# Revit family: 46-70-010-DN50-600
name_source: partatom
category: Pipe Accessories
units: mm (PartAtom-declared; Revit-internal decimal feet)

## family parameters
Always vertical = No
Cut with Voids When Loaded = No
Part Type = Valve - Breaks Into
Round Connector Dimension = Use Diameter
Shared = No
Work Plane-Based = No

## types (10) — shared parameters
46-050-70-01280 = DN050_PN16
46-080-70-01280 = DN080_PN16
46-100-70-01280 = DN100_PN16
46-150-70-01280 = DN150_PN16
46-200-70-01280 = DN200_PN16
46-250-70-01280 = DN250_PN16
46-300-70-01380 = DN300_PN16
46-400-70-01380 = DN400_PN16
46-500-70-01380 = DN500_PN16
46-600-70-01380 = DN600_PN16
Body_Wallthickness = 15 mm  [stored 0.0492126 ft]
Description_ = AVK GATE VALVE, LONG SPIGOT ENDS
Ftc = 4 mm  [stored 0.0131234 ft]
Name_Height_reference = 10 mm  [stored 0.0328084 ft]
Rib_Thickness = 18 mm  [stored 0.0590551 ft]
Search_table = 46-70-010-DN50-600
URL product pages = https://www.avkvalves.com

## per-type parameters (varying)
- DN050_PN16: At=45 mm  [stored 0.147638 ft]; Body_Height=101 mm; Body_depth=90 mm; Body_width=72 mm; Body_width_ref=86 mm; Bonnet_Flange_Depth=118 mm; Bonnet_Flange_Width=82 mm; Bonnet_Flange_cut=8 mm  [stored 0.0262467 ft]; Bonnet_Flange_thickness=15 mm  [stored 0.0492126 ft]; Bonnet_Reference_height=91 mm; Bonnet_Thickness=73 mm; Bt=73 mm; Bt_2=66 mm; CL _Thickness=25 mm  [stored 0.082021 ft]; CL_Height=50 mm; Cut_Reference=1140 mm; D=60 mm; D2=29 mm  [stored 0.0951444 ft]; D_ref=35 mm  [stored 0.114829 ft]; D_ref_2=30 mm  [stored 0.0984252 ft]; E=11 mm  [stored 0.0360892 ft]; F=7 mm  [stored 0.0229659 ft]; F1=8 mm  [stored 0.0262467 ft]; F1_ref=16 mm  [stored 0.0524934 ft]; Fillet_Thickness=6 mm  [stored 0.019685 ft]; Flange_Thickness=19 mm  [stored 0.062336 ft]; H=241 mm; H1=212 mm; H3=279 mm; H3_ref=38 mm  [stored 0.124672 ft]; Horizontal_Flange_width=76 mm; ID=25 mm  [stored 0.082021 ft]; L=570 mm; L2=125 mm; L_Dia=50 mm; L_ref=285 mm; Name_Reference=71 mm; Name_Width=36 mm  [stored 0.11811 ft]; Neck_H=62 mm; Neck_T=23 mm  [stored 0.0754593 ft]; Neck_T2=21 mm; Nominal Diameter (DN)=50 mm; R2f=15 mm  [stored 0.0492126 ft]; Rf=127 mm; Rib_Width_3=36 mm  [stored 0.11811 ft]; Rib_depth_3=36 mm  [stored 0.11811 ft]; S=3 mm  [stored 0.00984252 ft]
- DN080_PN16: At=70 mm; Body_Height=132 mm; Body_depth=140 mm; Body_width=75 mm; Body_width_ref=90 mm; Bonnet_Flange_Depth=171 mm; Bonnet_Flange_Width=90 mm; Bonnet_Flange_cut=8 mm  [stored 0.0262467 ft]; Bonnet_Flange_thickness=15 mm  [stored 0.0492126 ft]; Bonnet_Reference_height=122 mm; Bonnet_Thickness=77 mm; Bt=77 mm; Bt_2=69 mm; CL _Thickness=27 mm  [stored 0.0885827 ft]; CL_Height=75 mm; Cut_Reference=1100 mm; D=89 mm; D2=34 mm  [stored 0.111549 ft]; D_ref=50 mm; D_ref_2=44 mm  [stored 0.144357 ft]; E=15 mm  [stored 0.0492126 ft]; F=9 mm; F1=10 mm  [stored 0.0328084 ft]; F1_ref=20 mm  [stored 0.0656168 ft]; Fillet_Thickness=6 mm  [stored 0.019685 ft]; Flange_Thickness=19 mm  [stored 0.062336 ft]; H=297 mm; H1=263 mm; H3=350 mm; H3_ref=53 mm; Horizontal_Flange_width=106 mm; ID=40 mm  [stored 0.131234 ft]; L=550 mm; L2=140 mm; L_Dia=80 mm; L_ref=275 mm; Name_Reference=90 mm; Name_Width=38 mm  [stored 0.124672 ft]; Neck_H=56 mm; Neck_T=25 mm  [stored 0.082021 ft]; Neck_T2=23 mm  [stored 0.0754593 ft]; Nominal Diameter (DN)=80 mm; R2f=15 mm  [stored 0.0492126 ft]; Rf=177 mm; Rib_Width_3=38 mm  [stored 0.124672 ft]; Rib_depth_3=38 mm  [stored 0.124672 ft]; S=3 mm  [stored 0.00984252 ft]
- DN100_PN16: At=83 mm; Body_Height=148 mm; Body_depth=166 mm; Body_width=80 mm; Body_width_ref=96 mm; Bonnet_Flange_Depth=192 mm; Bonnet_Flange_Width=100 mm; Bonnet_Flange_cut=8 mm  [stored 0.0262467 ft]; Bonnet_Flange_thickness=15 mm  [stored 0.0492126 ft]; Bonnet_Reference_height=138 mm; Bonnet_Thickness=82 mm; Bt=82 mm; Bt_2=74 mm; CL _Thickness=29 mm  [stored 0.0951444 ft]; CL_Height=88 mm; Cut_Reference=1040 mm; D=114 mm; D2=38 mm  [stored 0.124672 ft]; D_ref=60 mm; D_ref_2=57 mm; E=15 mm  [stored 0.0492126 ft]; F=9 mm; F1=10 mm  [stored 0.0328084 ft]; F1_ref=20 mm  [stored 0.0656168 ft]; Fillet_Thickness=6 mm  [stored 0.019685 ft]; Flange_Thickness=19 mm  [stored 0.062336 ft]; H=334 mm; H1=296 mm; H3=398 mm; H3_ref=64 mm; Horizontal_Flange_width=128 mm; ID=50 mm; L=520 mm; L2=150 mm; L_Dia=100 mm; L_ref=260 mm; Name_Reference=101 mm; Name_Width=40 mm  [stored 0.131234 ft]; Neck_H=60 mm; Neck_T=27 mm  [stored 0.0885827 ft]; Neck_T2=25 mm  [stored 0.082021 ft]; Nominal Diameter (DN)=100 mm; R2f=15 mm  [stored 0.0492126 ft]; Rf=213 mm; Rib_Width_3=40 mm  [stored 0.131234 ft]; Rib_depth_3=40 mm  [stored 0.131234 ft]; S=4 mm  [stored 0.0131234 ft]
- DN150_PN16: At=121 mm; Body_Height=220 mm; Body_depth=242 mm; Body_width=95 mm; Body_width_ref=114 mm; Bonnet_Flange_Depth=272 mm; Bonnet_Flange_Width=130 mm; Bonnet_Flange_cut=8 mm  [stored 0.0262467 ft]; Bonnet_Flange_thickness=15 mm  [stored 0.0492126 ft]; Bonnet_Reference_height=210 mm; Bonnet_Thickness=97 mm; Bt=97 mm; Bt_2=89 mm; CL _Thickness=34 mm  [stored 0.111549 ft]; CL_Height=126 mm; Cut_Reference=1060 mm; D=168 mm; D2=38 mm  [stored 0.124672 ft]; D_ref=85 mm; D_ref_2=84 mm; E=15 mm  [stored 0.0492126 ft]; F=10 mm  [stored 0.0328084 ft]; F1=11 mm  [stored 0.0360892 ft]; F1_ref=22 mm  [stored 0.0721785 ft]; Fillet_Thickness=12 mm  [stored 0.0393701 ft]; Flange_Thickness=19 mm  [stored 0.062336 ft]; H=448 mm; H1=410 mm; H3=538 mm; H3_ref=90 mm; Horizontal_Flange_width=180 mm; ID=75 mm; L=530 mm; L2=175 mm; L_Dia=150 mm; L_ref=265 mm; Name_Reference=143 mm; Name_Width=48 mm; Neck_H=64 mm; Neck_T=32 mm  [stored 0.104987 ft]; Neck_T2=30 mm  [stored 0.0984252 ft]; Nominal Diameter (DN)=150 mm; R2f=30 mm  [stored 0.0984252 ft]; Rf=300 mm; Rib_Width_3=48 mm; Rib_depth_3=48 mm; S=5 mm  [stored 0.0164042 ft]
- DN200_PN16: At=147 mm; Body_Height=260 mm; Body_depth=294 mm; Body_width=108 mm; Body_width_ref=130 mm; Bonnet_Flange_Depth=332 mm; Bonnet_Flange_Width=140 mm; Bonnet_Flange_cut=13 mm; Bonnet_Flange_thickness=25 mm  [stored 0.082021 ft]; Bonnet_Reference_height=250 mm; Bonnet_Thickness=110 mm; Bt=110 mm; Bt_2=102 mm; CL _Thickness=34 mm  [stored 0.111549 ft]; CL_Height=152 mm; Cut_Reference=1140 mm; D=219 mm; D2=42 mm  [stored 0.137795 ft]; D_ref=110 mm; D_ref_2=110 mm; E=15 mm  [stored 0.0492126 ft]; F=12 mm  [stored 0.0393701 ft]; F1=14 mm  [stored 0.0459318 ft]; F1_ref=28 mm  [stored 0.0918635 ft]; Fillet_Thickness=24 mm  [stored 0.0787402 ft]; Flange_Thickness=20 mm  [stored 0.0656168 ft]; H=562 mm; H1=520 mm; H3=680 mm; H3_ref=118 mm; Horizontal_Flange_width=236 mm; ID=100 mm; L=570 mm; L2=200 mm; L_Dia=200 mm; L_ref=285 mm; Name_Reference=183 mm; Name_Width=54 mm; Neck_H=108 mm; Neck_T=32 mm  [stored 0.104987 ft]; Neck_T2=30 mm  [stored 0.0984252 ft]; Nominal Diameter (DN)=200 mm; R2f=60 mm; Rf=393 mm; Rib_Width_3=54 mm; Rib_depth_3=54 mm; S=6 mm  [stored 0.019685 ft]
- DN250_PN16: At=196 mm; Body_Height=320 mm; Body_depth=392 mm; Body_width=132 mm; Body_width_ref=158 mm; Bonnet_Flange_Depth=422 mm; Bonnet_Flange_Width=175 mm; Bonnet_Flange_cut=13 mm; Bonnet_Flange_thickness=25 mm  [stored 0.082021 ft]; Bonnet_Reference_height=310 mm; Bonnet_Thickness=135 mm; Bt=135 mm; Bt_2=126 mm; CL _Thickness=46 mm  [stored 0.150919 ft]; CL_Height=201 mm; Cut_Reference=1180 mm; D=273 mm; D2=47 mm  [stored 0.154199 ft]; D_ref=135 mm; D_ref_2=137 mm; E=15 mm  [stored 0.0492126 ft]; F=14 mm  [stored 0.0459318 ft]; F1=16 mm  [stored 0.0524934 ft]; F1_ref=31 mm  [stored 0.101706 ft]; Fillet_Thickness=24 mm  [stored 0.0787402 ft]; Flange_Thickness=22 mm  [stored 0.0721785 ft]; H=664 mm; H1=617 mm; H3=811 mm; H3_ref=147 mm; Horizontal_Flange_width=294 mm; ID=125 mm; L=590 mm; L2=200 mm; L_Dia=250 mm; L_ref=295 mm; Name_Reference=200 mm; Name_Width=66 mm; Neck_H=96 mm; Neck_T=44 mm  [stored 0.144357 ft]; Neck_T2=42 mm  [stored 0.137795 ft]; Nominal Diameter (DN)=250 mm; R2f=60 mm; Rf=490 mm; Rib_Width_3=66 mm; Rib_depth_3=66 mm; S=6 mm  [stored 0.019685 ft]
- DN300_PN16: At=209 mm; Body_Height=415 mm; Body_depth=418 mm; Body_width=160 mm; Body_width_ref=192 mm; Bonnet_Flange_Depth=448 mm; Bonnet_Flange_Width=200 mm; Bonnet_Flange_cut=18 mm  [stored 0.0590551 ft]; Bonnet_Flange_thickness=35 mm  [stored 0.114829 ft]; Bonnet_Reference_height=405 mm; Bonnet_Thickness=163 mm; Bt=163 mm; Bt_2=154 mm; CL _Thickness=60 mm; CL_Height=214 mm; Cut_Reference=1240 mm; D=324 mm; D2=47 mm  [stored 0.154199 ft]; D_ref=160 mm; D_ref_2=162 mm; E=15 mm  [stored 0.0492126 ft]; F=14 mm  [stored 0.0459318 ft]; F1=16 mm  [stored 0.0524934 ft]; F1_ref=31 mm  [stored 0.101706 ft]; Fillet_Thickness=24 mm  [stored 0.0787402 ft]; Flange_Thickness=25 mm  [stored 0.082021 ft]; H=740 mm; H1=693 mm; H3=911 mm; H3_ref=171 mm; Horizontal_Flange_width=342 mm; ID=150 mm; L=620 mm; L2=200 mm; L_Dia=300 mm; L_ref=310 mm; Name_Reference=300 mm; Name_Width=80 mm; Neck_H=64 mm; Neck_T=58 mm; Neck_T2=56 mm; Nominal Diameter (DN)=300 mm; R2f=60 mm; Rf=570 mm; Rib_Width_3=80 mm; Rib_depth_3=80 mm; S=7 mm  [stored 0.0229659 ft]
- DN400_PN16: At=238 mm; Body_Height=550 mm; Body_depth=476 mm; Body_width=150 mm; Body_width_ref=180 mm; Bonnet_Flange_Depth=550 mm; Bonnet_Flange_Width=170 mm; Bonnet_Flange_cut=35 mm  [stored 0.114829 ft]; Bonnet_Flange_thickness=70 mm; Bonnet_Reference_height=540 mm; Bonnet_Thickness=153 mm; Bt=153 mm; Bt_2=144 mm; CL _Thickness=51 mm; CL_Height=243 mm; Cut_Reference=1352 mm; D=406 mm; D2=55 mm; D_ref=210 mm; D_ref_2=203 mm; E=15 mm  [stored 0.0492126 ft]; F=16 mm  [stored 0.0524934 ft]; F1=19 mm  [stored 0.062336 ft]; F1_ref=37 mm  [stored 0.121391 ft]; Fillet_Thickness=32 mm  [stored 0.104987 ft]; Flange_Thickness=28 mm  [stored 0.0918635 ft]; H=939 mm; H1=884 mm; H3=1139 mm; H3_ref=200 mm; Horizontal_Flange_width=400 mm; ID=200 mm; L=676 mm; L2=200 mm; L_Dia=400 mm; L_ref=338 mm; Name_Reference=475 mm; Name_Width=75 mm; Neck_H=91 mm; Neck_T=49 mm; Neck_T2=47 mm  [stored 0.154199 ft]; Nominal Diameter (DN)=400 mm; R2f=80 mm; Rf=667 mm; Rib_Width_3=0 mm  [stored 0 ft]; Rib_depth_3=0 mm  [stored 0 ft]; S=9 mm
- DN500_PN16: At=360 mm; Body_Height=600 mm; Body_depth=719 mm; Body_width=187 mm; Body_width_ref=224 mm; Bonnet_Flange_Depth=792 mm; Bonnet_Flange_Width=219 mm; Bonnet_Flange_cut=35 mm  [stored 0.114829 ft]; Bonnet_Flange_thickness=70 mm; Bonnet_Reference_height=590 mm; Bonnet_Thickness=191 mm; Bt=191 mm; Bt_2=181 mm; CL _Thickness=70 mm; CL_Height=365 mm; Cut_Reference=1452 mm; D=508 mm; D2=75 mm; D_ref=260 mm; D_ref_2=254 mm; E=15 mm  [stored 0.0492126 ft]; F=15 mm  [stored 0.0492126 ft]; F1=19 mm  [stored 0.062336 ft]; F1_ref=37 mm  [stored 0.121391 ft]; Fillet_Thickness=32 mm  [stored 0.104987 ft]; Flange_Thickness=32 mm  [stored 0.104987 ft]; H=1133 mm; H1=1058 mm; H3=1446 mm; H3_ref=313 mm; Horizontal_Flange_width=626 mm; ID=250 mm; L=726 mm; L2=200 mm; L_Dia=500 mm; L_ref=363 mm; Name_Reference=590 mm; Name_Width=94 mm; Neck_H=94 mm; Neck_T=68 mm; Neck_T2=66 mm; Nominal Diameter (DN)=500 mm; R2f=80 mm; Rf=1043 mm; Rib_Width_3=0 mm  [stored 0 ft]; Rib_depth_3=0 mm  [stored 0 ft]; S=11 mm  [stored 0.0360892 ft]
- DN600_PN16: At=408 mm; Body_Height=740 mm; Body_depth=815 mm; Body_width=210 mm; Body_width_ref=252 mm; Bonnet_Flange_Depth=891 mm; Bonnet_Flange_Width=247 mm; Bonnet_Flange_cut=35 mm  [stored 0.114829 ft]; Bonnet_Flange_thickness=70 mm; Bonnet_Reference_height=730 mm; Bonnet_Thickness=214 mm; Bt=214 mm; Bt_2=204 mm; CL _Thickness=81 mm; CL_Height=413 mm; Cut_Reference=1552 mm; D=610 mm; D2=75 mm; D_ref=310 mm; D_ref_2=305 mm; E=15 mm  [stored 0.0492126 ft]; F=15 mm  [stored 0.0492126 ft]; F1=19 mm  [stored 0.062336 ft]; F1_ref=37 mm  [stored 0.121391 ft]; Fillet_Thickness=32 mm  [stored 0.104987 ft]; Flange_Thickness=36 mm  [stored 0.11811 ft]; H=1276 mm; H1=1201 mm; H3=1646 mm; H3_ref=370 mm; Horizontal_Flange_width=740 mm; ID=300 mm; L=776 mm; L2=200 mm; L_Dia=600 mm; L_ref=388 mm; Name_Reference=655 mm; Name_Width=105 mm; Neck_H=49 mm; Neck_T=79 mm; Neck_T2=77 mm; Nominal Diameter (DN)=600 mm; R2f=80 mm; Rf=1233 mm; Rib_Width_3=0 mm  [stored 0 ft]; Rib_depth_3=0 mm  [stored 0 ft]; S=13 mm

note: [stored X ft] marks values corroborated as IEEE doubles in the binary element streams (Revit-internal decimal feet)

## geometry (parser evidence)
native form markers: Extrusion x1, Sweep x2
no freeform markers — native parametric forms only
